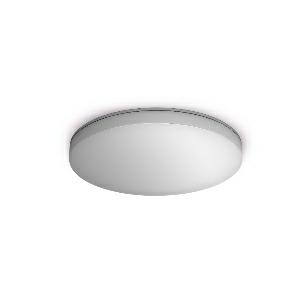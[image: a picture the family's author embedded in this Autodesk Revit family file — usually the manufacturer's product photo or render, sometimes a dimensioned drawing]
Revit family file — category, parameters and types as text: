
# Revit family: rs_pro_connect_r10_057046
name_source: partatom
category: Leuchten
revit_build: Autodesk Revit 2016 (Build: 20190508_0715(x64)
units: mm (PartAtom-declared; Revit-internal decimal feet)

## family parameters
Basisbauteil = Fläche
Beim Laden mit Abzugskörper schneiden = Nein
Bemaßung runder Anschluss = Durchmesser verwenden
Gemeinsam genutzt = Nein
Lichtquelle = Nein
Raumberechnungspunkt = Nein
Teiletyp = Normal

## types (1)
- RS PRO Connect R10 (1 x , 1130 lm, 4000 K)
    Beschreibung = Dimensions (Ø x H): 300 x 55 mm; Mains power supply: 220 – 240 V / 50 – 60 Hz; Sensor Technology: High frequency; Transmitter power: < 1 mW; HF-system: 5,8 GHz; Output: 9 W; Interconnection: Yes; Type of interconnection: Master/slave; Luminous flux: 1130 lm; Colour temperature: 4000 K; Colour variation LED: SDCM3; Colour Rendering Index CRI: 80-89; With lamp: Yes, STEINEL LED system; Lamp: LED cannot be replaced; LED life expectancy (max. °C): 55000 h; LED life expectancy (25 °C): 60000 h; Drop in luminous flux in accordance with LM80: L80B50; Base: without; LED cooling system: Passive Thermo Control; With motion detector: Yes; Detection: also through glass, wood and stud walls; Detection angle: 360 °; Angle of aperture: 160 °; Capability of masking out individual segments: Yes; Electronic scalability: Yes; Mechanical scalability: No; Reach, radial: Ø 10 m (79 m²); Reach, tangential: Ø 10 m (79 m²); Main light adjustable: 50 - 100 %; Continuous light: selectable; Photo-cell controller: Yes; Twilight setting: 2 – 2000 lx; Time setting: 5 sec – 30 min; Basic light level function: Yes; Basic light level function, detail: LED Backlight; Basic light level function time: 10-30 min, all night; Functions: Group parameterisation, Manual ON / ON-OFF, Master/slave override, Neighbouring-group function, Presence function, Backlight; Soft light start: Yes; Impact resistance: IK07; IP-rating: IP40; Protection class: II; Ambient temperature: -20 – 40 °C; Housing material: Plastic; Cover material: PC, opal; Manufacturer's Warranty: 5 years; Settings via: Bluetooth; With remote control: No; Version: Neutral white; PU1, EAN: 4007841057046
    CIE Flux Codes = 44 75 93 94 100
    Color Rendering = 80-89
    Color Temperature = 4000 K
    Frequency = 60 Hz, 50 Hz
    Height = 0 mm  [stored 0 ft]
    Hersteller = Steinel
    Lamp Light Flux = 1130 lm
    Lamp count = 1
    Lampe = 1 x
    Length = 300 mm
    Luminous efficacy = 0 lm/W
    ModVariant = Nein
    Modell = 057046
    Mounting Type = Surface mounted
    Number of Poles = 1
    OnlyDefault = Ja
    Power Factor = 1
    Product Name = RS PRO Connect R10
    Product group = Sensor-switched indoor light
    ProductGroupID = 30
    Protection Class = Protection class II
    Protection Degree = IP 40
    RlxData = <blob elided: 167929 chars, md5=12c8e044>
    Scheinlast = 0 VA
    Socket = socket
    Standby Power = 0 W
    System Light Flux = 0 lm
    System Power = 0 W
    Typenbild = produkt1_057046.jpg
    Typenkommentare = Product without accessories
    URL = http://relux.com
    VarID = ---
    Voltage = 0 V
    Vorgabe-Ansicht = 1800 mm
    Weight = 0.00 kg
    Width = 0 mm  [stored 0 ft]

note: [stored X ft] marks values corroborated as IEEE doubles in the binary element streams (Revit-internal decimal feet)

## geometry (parser evidence)
native form markers: Sweep x11
no freeform markers — native parametric forms only
